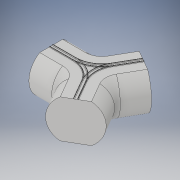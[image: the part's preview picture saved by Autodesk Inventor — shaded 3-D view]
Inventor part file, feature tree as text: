
AUTODESK INVENTOR PART (.ipt)
format: ipt  version: 2017 (Build 210142000, 142)  size: 360,960 bytes
history: native  units: in
note: dims shown in document units (in); Inventor stores cm internally (conversion verified against a paired STEP export)
features: sketch x4, extrude x2, other x2, pattern_circular x2, sweep x1
ambient origin geometry x8: Origin, YZ Plane, XZ Plane, XY Plane, X Axis, Y Axis, Z Axis, Center Point
bodies: Solid1 (feature_tree)
feature tree (11):
  sketch  "Sketch1"  dims[d10=6.6667in d12=4.0in d13=0.0in d15=2.8217in d16=1.1811in d17=360.0deg]
  extrude  "corridor"  Depth=2.8217in
  other  "found rotaion axis"
  other  "rotaion axis"
  pattern_circular  "other corridors"  Count=3 Angle=360.0deg
  sketch  "Sketch5"  dims[d105=4.0in d106=0.5833in d107=3.8873in d108=3.8873in d109=1.7083in d110=0.0625in d111=0.0625in d112=1.6458in d113=0.25in d114=0.125in d115=0.0892in d116=0.0884in d117=45.0deg d118=3.3333in d119=0.125in]
  sketch  "Sketch4"  dims[d24=0.0in d25=0.0in d26=1.1811in d27=360.0deg]
  sweep  "curve edjes"
  pattern_circular  "repeat curve edjes"  [2 undecoded]
  extrude  "hole fill in"  [1 undecoded]
  sketch  "Sketch10"  dims[d120=1.0in d121=0.0in]
note: 3 required parameter values undecoded (feature->parameter linkage not recoverable at this tier; creation-order binding heuristic only, values carry confidence <= 0.55)
